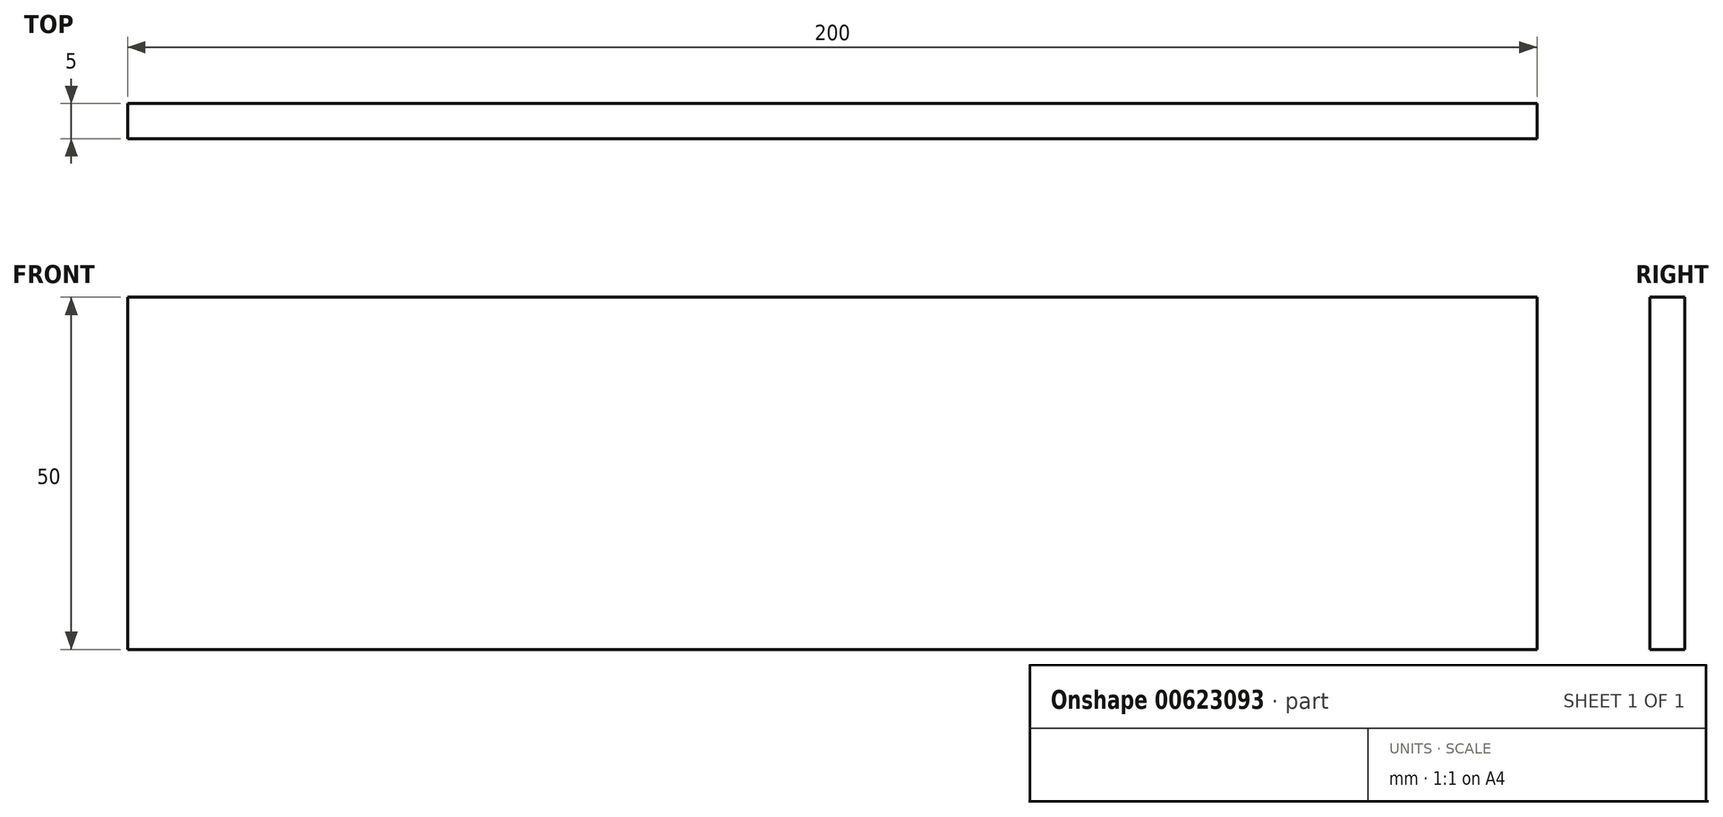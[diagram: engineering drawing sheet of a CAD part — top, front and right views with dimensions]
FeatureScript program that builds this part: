
annotation { "Feature Type Name" : "Feature", "Feature Type Description" : "" }
export const myFeature = defineFeature(function(context is Context, id is Id, definition is map)
    precondition{}
    {
        {
            var Q0;
            Q0=qCreatedBy(makeId("Front.planeOp"),FACE);
            var sketch = newSketch(context, id + "F0", { "sketchPlane" : qUnion([Q0])});
            skLineSegment(sketch, "E0.bottom", {"start": v(-200, 50) * mm, "end": v(0, 50) * mm});
            skLineSegment(sketch, "E0.top", {"start": v(-200, 0) * mm, "end": v(0, 0) * mm});
            skLineSegment(sketch, "E0.left", {"start": v(-200, 50) * mm, "end": v(-200, 0) * mm});
            skLineSegment(sketch, "E0.right", {"start": v(0, 50) * mm, "end": v(0, 0) * mm});
            skSolve(sketch);
        }
        {
            var Q0;
            Q0 = qSketchRegion(id + "F0", true);
            extrude(context, id + "F1", {"entities" : qUnion([Q0]), "depth" : 5 * mm, "offsetDistance" : 25 * mm});
        }
    });
